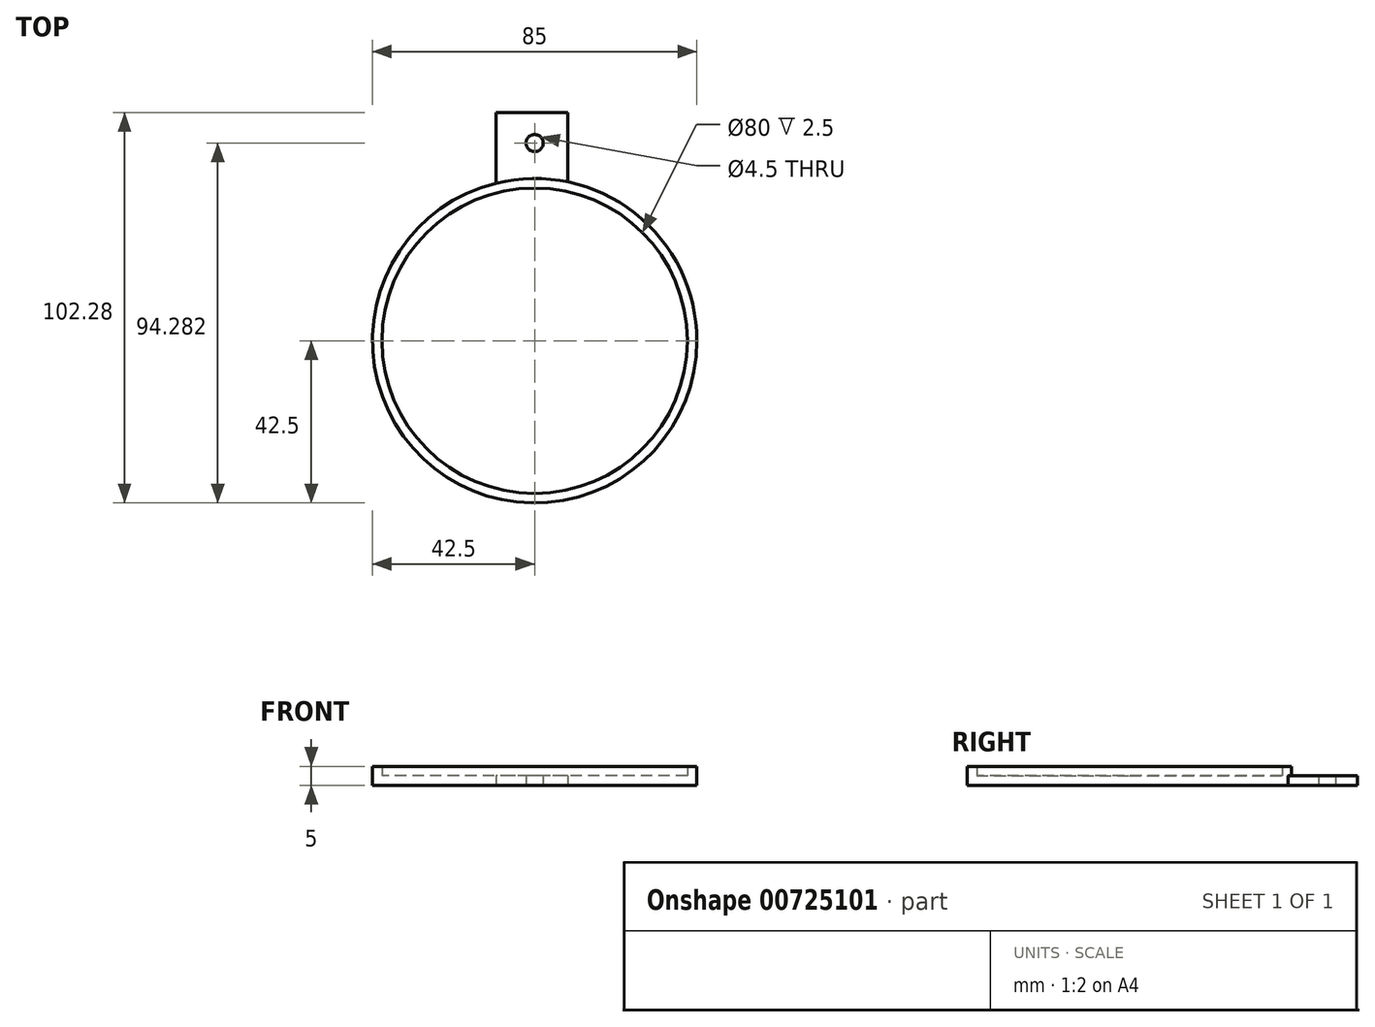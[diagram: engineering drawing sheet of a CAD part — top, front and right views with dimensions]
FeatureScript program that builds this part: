
annotation { "Feature Type Name" : "Feature", "Feature Type Description" : "" }
export const myFeature = defineFeature(function(context is Context, id is Id, definition is map)
    precondition{}
    {
        {
            var Q0;
            Q0=qCreatedBy(makeId("Top.planeOp"),FACE);
            var sketch = newSketch(context, id + "F0", { "sketchPlane" : qUnion([Q0])});
            skCircle(sketch, "E0", {"center": v(0, 0) * mm, "radius": 42.5 * mm});
            skLineSegment(sketch, "E1", {"start": v(8.73, 41.6) * mm, "end": v(8.73, 59.78) * mm});
            skLineSegment(sketch, "E2", {"start": v(8.73, 59.78) * mm, "end": v(-10.14, 59.78) * mm});
            skLineSegment(sketch, "E3", {"start": v(-10.14, 59.78) * mm, "end": v(-10.14, 41.27) * mm});
            skCircle(sketch, "E4.0", {"center": v(0, 0) * mm, "radius": 40 * mm});
            skPoint(sketch, "E5", {"position": v(0, 51.78) * mm});
            skSolve(sketch);
        }
        {
            var Q0;
            Q0=makeQuery(id+"F0.imprint","IMPRINT",FACE,{"disambiguationData":[TD([[makeQuery(id+"F0.imprint","IMPRINT",EDGE,{"derivedFrom":sQuery(id+"F0.wireOp",EDGE,"E4.0")}),-1.0]])]});
            extrude(context, id + "F1", {"entities" : qUnion([Q0]), "depth" : 5 * mm, "offsetDistance" : 25 * mm});
        }
        {
            var Q0;
            {var subQ0=sQuery(id+"F0.wireOp",EDGE,"E1");Q0=makeQuery(id+"F0.imprint","IMPRINT",FACE,{"disambiguationData":[TD([[makeQuery(id+"F0.imprint","IMPRINT",EDGE,{"derivedFrom":subQ0}),1.0]])]});}
            var Q1;
            Q1=makeQuery(id+"F0.imprint","IMPRINT",FACE,{"disambiguationData":[TD([[makeQuery(id+"F0.imprint","IMPRINT",EDGE,{"derivedFrom":sQuery(id+"F0.wireOp",EDGE,"E4.0")}),1.0]])]});
            extrude(context, id + "F2", {"entities" : qUnion([Q0, Q1]), "operationType" : NewBodyOperationType.ADD, "depth" : 2.5 * mm, "offsetDistance" : 25 * mm});
        }
        {
            var Q0;
            Q0=sQuery(id+"F0.wireOp",VERTEX,"E5");
            var Q1;
            Q1=makeQuery(id+"F1.opExtrude","SWEPT_BODY",BODY,{"disambiguationData":[OSD([sQuery(id+"F0.wireOp",EDGE,"E0"),sQuery(id+"F0.wireOp",EDGE,"E4.0")])]});
            hole(context, id + "F3", {"style" : HoleStyle.SIMPLE, "endStyle" : HoleEndStyle.THROUGH, "oppositeDirection" : true, "standardTappedOrClearance" : lookupTablePath({ "standard" : "ANSI", "fit" : "Normal (ASME)", "size" : "#8", "type" : "Clearance" }), "standardBlindInLast" : lookupTablePath({ "fit" : "Free", "standard" : "ANSI", "size" : "#8", "type" : "Clearance" }), "holeDiameter" : 4.5 * mm, "majorDiameter" : 5 * mm, "isTappedThrough" : true, "tappedDepth" : 12 * mm, "tapClearance" : 3, "locations" : qUnion([Q0]), "scope" : qUnion([Q1])});
        }
    });
